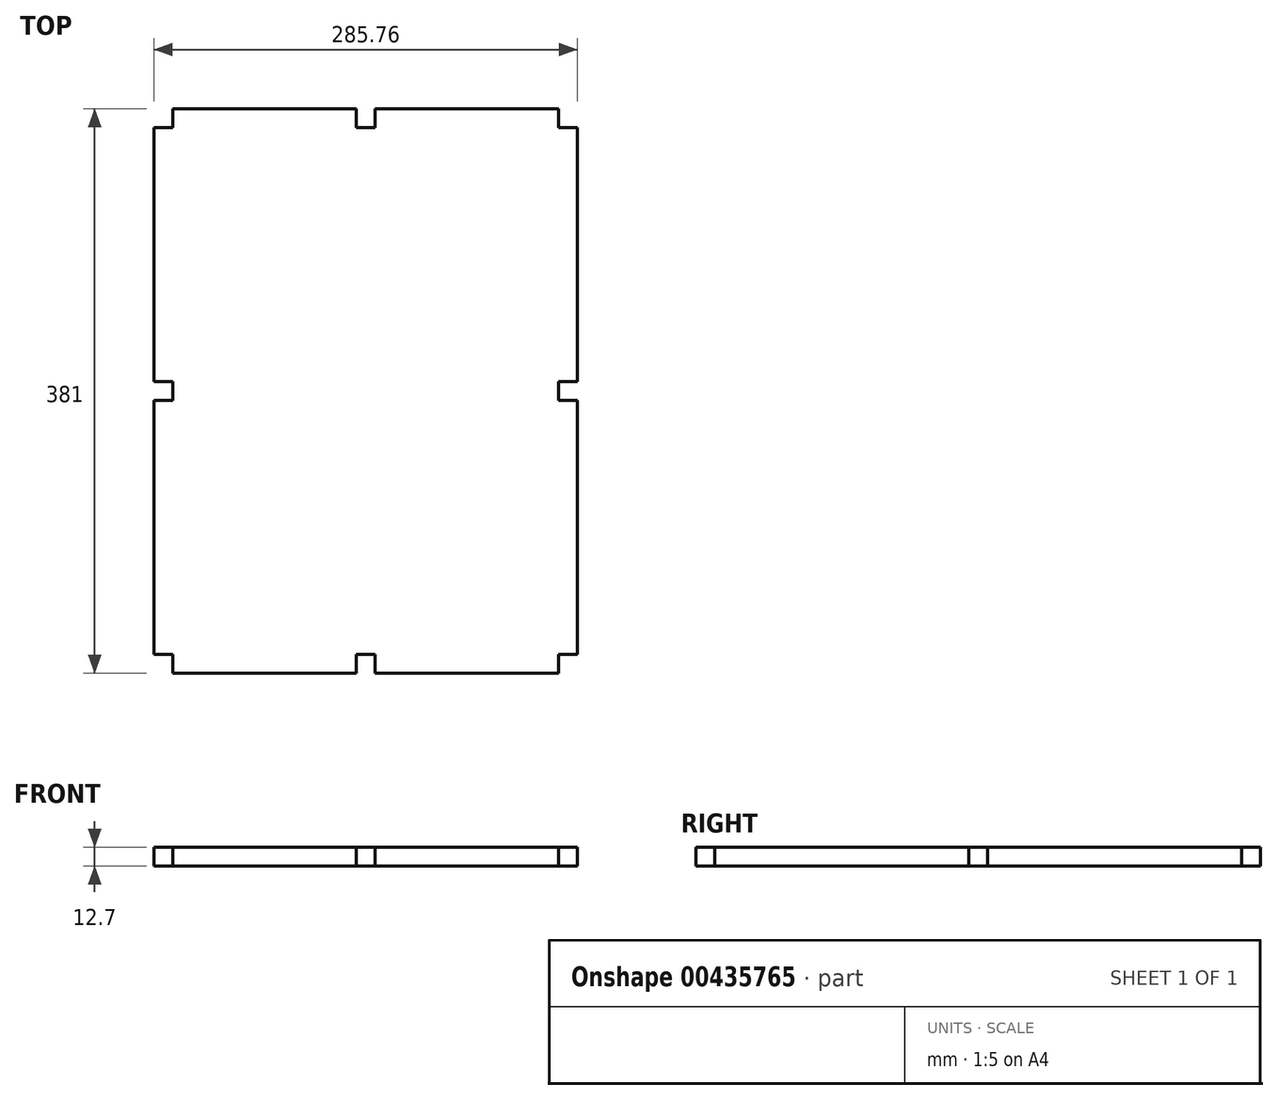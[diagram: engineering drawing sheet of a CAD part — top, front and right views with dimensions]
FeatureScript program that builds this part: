
annotation { "Feature Type Name" : "Feature", "Feature Type Description" : "" }
export const myFeature = defineFeature(function(context is Context, id is Id, definition is map)
    precondition{}
    {
        {
            var Q0;
            Q0=qCreatedBy(makeId("Top.planeOp"),FACE);
            var sketch = newSketch(context, id + "F0", { "sketchPlane" : qUnion([Q0])});
            skLineSegment(sketch, "E0.bottom", {"start": v(-130.18, 0) * mm, "end": v(-6.35, 0) * mm});
            skLineSegment(sketch, "E0.top", {"start": v(-130.17, -381) * mm, "end": v(-6.35, -381) * mm});
            skLineSegment(sketch, "E0.left", {"start": v(-142.88, -12.7) * mm, "end": v(-142.88, -184.15) * mm});
            skLineSegment(sketch, "E0.right", {"start": v(142.87, -12.7) * mm, "end": v(142.88, -184.15) * mm});
            skLineSegment(sketch, "E1", {"start": v(-142.88, -12.7) * mm, "end": v(-130.18, -12.7) * mm});
            skLineSegment(sketch, "E2", {"start": v(-130.18, -12.7) * mm, "end": v(-130.18, 0) * mm});
            skLineSegment(sketch, "E3", {"start": v(130.17, 0) * mm, "end": v(130.17, -12.7) * mm});
            skLineSegment(sketch, "E4", {"start": v(130.17, -12.7) * mm, "end": v(142.87, -12.7) * mm});
            skLineSegment(sketch, "E5", {"start": v(-142.88, -368.3) * mm, "end": v(-130.17, -368.3) * mm});
            skLineSegment(sketch, "E6", {"start": v(-130.18, -368.3) * mm, "end": v(-130.18, -381) * mm});
            skLineSegment(sketch, "E7", {"start": v(130.18, -381) * mm, "end": v(130.18, -368.3) * mm});
            skLineSegment(sketch, "E8", {"start": v(130.18, -368.3) * mm, "end": v(142.88, -368.3) * mm});
            skLineSegment(sketch, "E9.trimOffspring", {"start": v(-142.88, -196.85) * mm, "end": v(-142.88, -368.3) * mm});
            skLineSegment(sketch, "E10.trimOffspring", {"start": v(142.88, -196.85) * mm, "end": v(142.88, -368.3) * mm});
            skLineSegment(sketch, "E11", {"start": v(-6.35, 0) * mm, "end": v(-6.35, -12.7) * mm});
            skLineSegment(sketch, "E12", {"start": v(-6.35, -12.7) * mm, "end": v(6.35, -12.7) * mm});
            skLineSegment(sketch, "E13", {"start": v(6.35, -12.7) * mm, "end": v(6.35, 0) * mm});
            skLineSegment(sketch, "E14", {"start": v(-6.35, -381) * mm, "end": v(-6.35, -368.3) * mm});
            skLineSegment(sketch, "E15", {"start": v(-6.35, -368.3) * mm, "end": v(6.35, -368.3) * mm});
            skLineSegment(sketch, "E16", {"start": v(6.35, -368.3) * mm, "end": v(6.35, -381) * mm});
            skLineSegment(sketch, "E17.trimOffspring", {"start": v(6.35, 0) * mm, "end": v(130.17, 0) * mm});
            skLineSegment(sketch, "E18.trimOffspring", {"start": v(6.35, -381) * mm, "end": v(130.18, -381) * mm});
            skPoint(sketch, "E19", {"position": v(0, -190.5) * mm});
            skLineSegment(sketch, "E20", {"start": v(142.88, -184.15) * mm, "end": v(130.18, -184.15) * mm});
            skLineSegment(sketch, "E21", {"start": v(130.17, -184.15) * mm, "end": v(130.17, -196.85) * mm});
            skLineSegment(sketch, "E22", {"start": v(130.18, -196.85) * mm, "end": v(142.88, -196.85) * mm});
            skLineSegment(sketch, "E23", {"start": v(-142.88, -184.15) * mm, "end": v(-130.18, -184.15) * mm});
            skLineSegment(sketch, "E24", {"start": v(-130.18, -184.15) * mm, "end": v(-130.18, -196.85) * mm});
            skLineSegment(sketch, "E25", {"start": v(-130.18, -196.85) * mm, "end": v(-142.88, -196.85) * mm});
            skSolve(sketch);
        }
        {
            var Q0;
            Q0=makeQuery(id+"F0.imprint","IMPRINT",FACE,{"disambiguationData":[TD([[makeQuery(id+"F0.imprint","IMPRINT",EDGE,{"derivedFrom":sQuery(id+"F0.wireOp",EDGE,"E0.bottom")}),-1.0]])]});
            extrude(context, id + "F1", {"entities" : qUnion([Q0]), "depth" : 12.7 * mm});
        }
    });
